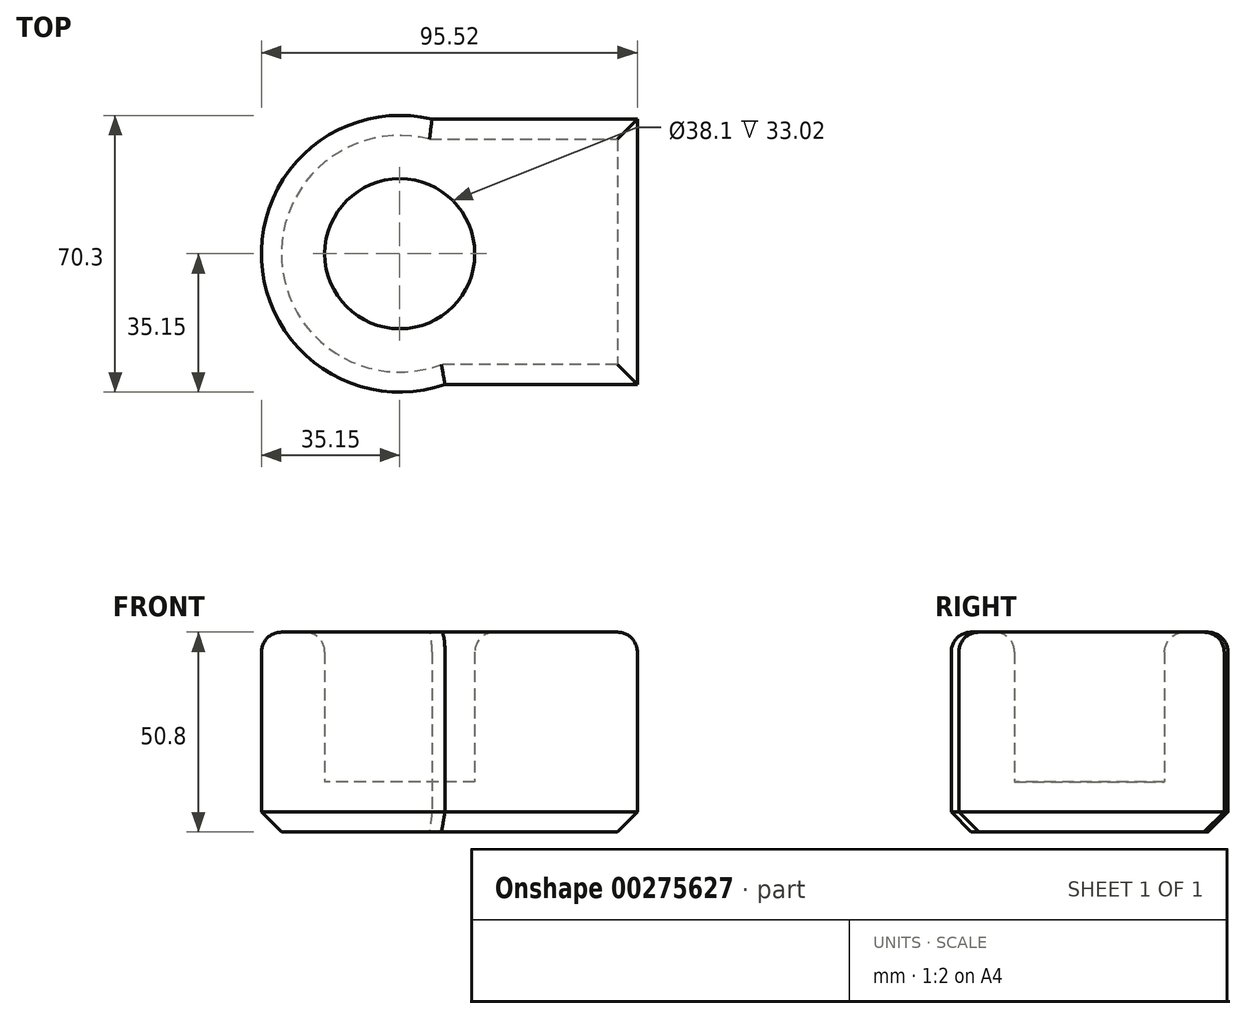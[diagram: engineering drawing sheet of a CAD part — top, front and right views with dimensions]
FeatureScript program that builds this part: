
annotation { "Feature Type Name" : "Feature", "Feature Type Description" : "" }
export const myFeature = defineFeature(function(context is Context, id is Id, definition is map)
    precondition{}
    {
        {
            var Q0;
            Q0=qCreatedBy(makeId("Top.planeOp"),FACE);
            var sketch = newSketch(context, id + "F0", { "sketchPlane" : qUnion([Q0])});
            skCircle(sketch, "E0", {"center": v(0, 0) * mm, "radius": 35.15 * mm});
            skLineSegment(sketch, "E1.bottom", {"start": v(8.17, 34.19) * mm, "end": v(60.37, 34.19) * mm});
            skLineSegment(sketch, "E1.top", {"start": v(8.17, -33.23) * mm, "end": v(60.37, -33.23) * mm});
            skLineSegment(sketch, "E1.left", {"start": v(8.17, 34.19) * mm, "end": v(8.17, -33.23) * mm});
            skLineSegment(sketch, "E1.right", {"start": v(60.37, 34.19) * mm, "end": v(60.37, -33.23) * mm});
            skCircle(sketch, "E2", {"center": v(0, 0) * mm, "radius": 19.05 * mm});
            skSolve(sketch);
        }
        {
            var Q0;
            Q0 = qSketchRegion(id + "F0", true);
            extrude(context, id + "F1", {"entities" : qUnion([Q0]), "depth" : 50.8 * mm});
        }
        {
            var Q0;
            Q0=makeQuery(id+"F1.opExtrude","CAP_EDGE",EDGE,{"disambiguationData":[OSD([sQuery(id+"F0.wireOp",EDGE,"E0")])],"isStart":true});
            var Q1;
            Q1=makeQuery(id+"F1.opExtrude","CAP_EDGE",EDGE,{"disambiguationData":[OSD([sQuery(id+"F0.wireOp",EDGE,"E1.bottom")])],"isStart":true});
            var Q2;
            Q2=makeQuery(id+"F1.opExtrude","CAP_EDGE",EDGE,{"disambiguationData":[OSD([sQuery(id+"F0.wireOp",EDGE,"E1.right")])],"isStart":true});
            var Q3;
            Q3=makeQuery(id+"F1.opExtrude","CAP_EDGE",EDGE,{"disambiguationData":[OSD([sQuery(id+"F0.wireOp",EDGE,"E1.top")])],"isStart":true});
            chamfer(context, id + "F2", {"entities" : qUnion([Q0, Q1, Q2, Q3]), "width" : 5.08 * mm, "tangentPropagation" : true});
        }
        {
            var Q0;
            Q0=qCreatedBy(makeId("Top.planeOp"),FACE);
            var sketch = newSketch(context, id + "F3", { "sketchPlane" : qUnion([Q0])});
            skCircle(sketch, "E3", {"center": v(0, 0) * mm, "radius": 27.92 * mm});
            skLineSegment(sketch, "E4.bottom", {"start": v(9.96, -26.08) * mm, "end": v(51.61, -26.08) * mm});
            skLineSegment(sketch, "E4.top", {"start": v(9.96, 26.86) * mm, "end": v(51.61, 26.86) * mm});
            skLineSegment(sketch, "E4.left", {"start": v(9.96, -26.08) * mm, "end": v(9.96, 26.86) * mm});
            skLineSegment(sketch, "E4.right", {"start": v(51.61, -26.08) * mm, "end": v(51.61, 26.86) * mm});
            skSolve(sketch);
        }
        {
            var Q0;
            Q0 = qSketchRegion(id + "F3", true);
            extrude(context, id + "F4", {"entities" : qUnion([Q0]), "operationType" : NewBodyOperationType.ADD, "depth" : 12.7 * mm});
        }
        {
            var Q0;
            Q0=makeQuery(id+"F1.opExtrude","CAP_EDGE",EDGE,{"disambiguationData":[OSD([sQuery(id+"F0.wireOp",EDGE,"E0")])],"isStart":false});
            var Q1;
            Q1=makeQuery(id+"F1.opExtrude","CAP_EDGE",EDGE,{"disambiguationData":[OSD([sQuery(id+"F0.wireOp",EDGE,"E1.top")])],"isStart":false});
            var Q2;
            Q2=makeQuery(id+"F1.opExtrude","CAP_EDGE",EDGE,{"disambiguationData":[OSD([sQuery(id+"F0.wireOp",EDGE,"E1.right")])],"isStart":false});
            var Q3;
            Q3=makeQuery(id+"F1.opExtrude","CAP_EDGE",EDGE,{"disambiguationData":[OSD([sQuery(id+"F0.wireOp",EDGE,"E1.bottom")])],"isStart":false});
            fillet(context, id + "F5", {"entities" : qUnion([Q0, Q1, Q2, Q3]), "radius" : 5.08 * mm, "tangentPropagation" : true, "allowEdgeOverflow" : false});
        }
        {
            var Q0;
            Q0=makeQuery(id+"F1.opExtrude","CAP_EDGE",EDGE,{"disambiguationData":[OSD([sQuery(id+"F0.wireOp",EDGE,"E2")])],"isStart":false});
            fillet(context, id + "F6", {"entities" : qUnion([Q0]), "radius" : 5.08 * mm, "tangentPropagation" : true, "allowEdgeOverflow" : false});
        }
    });
